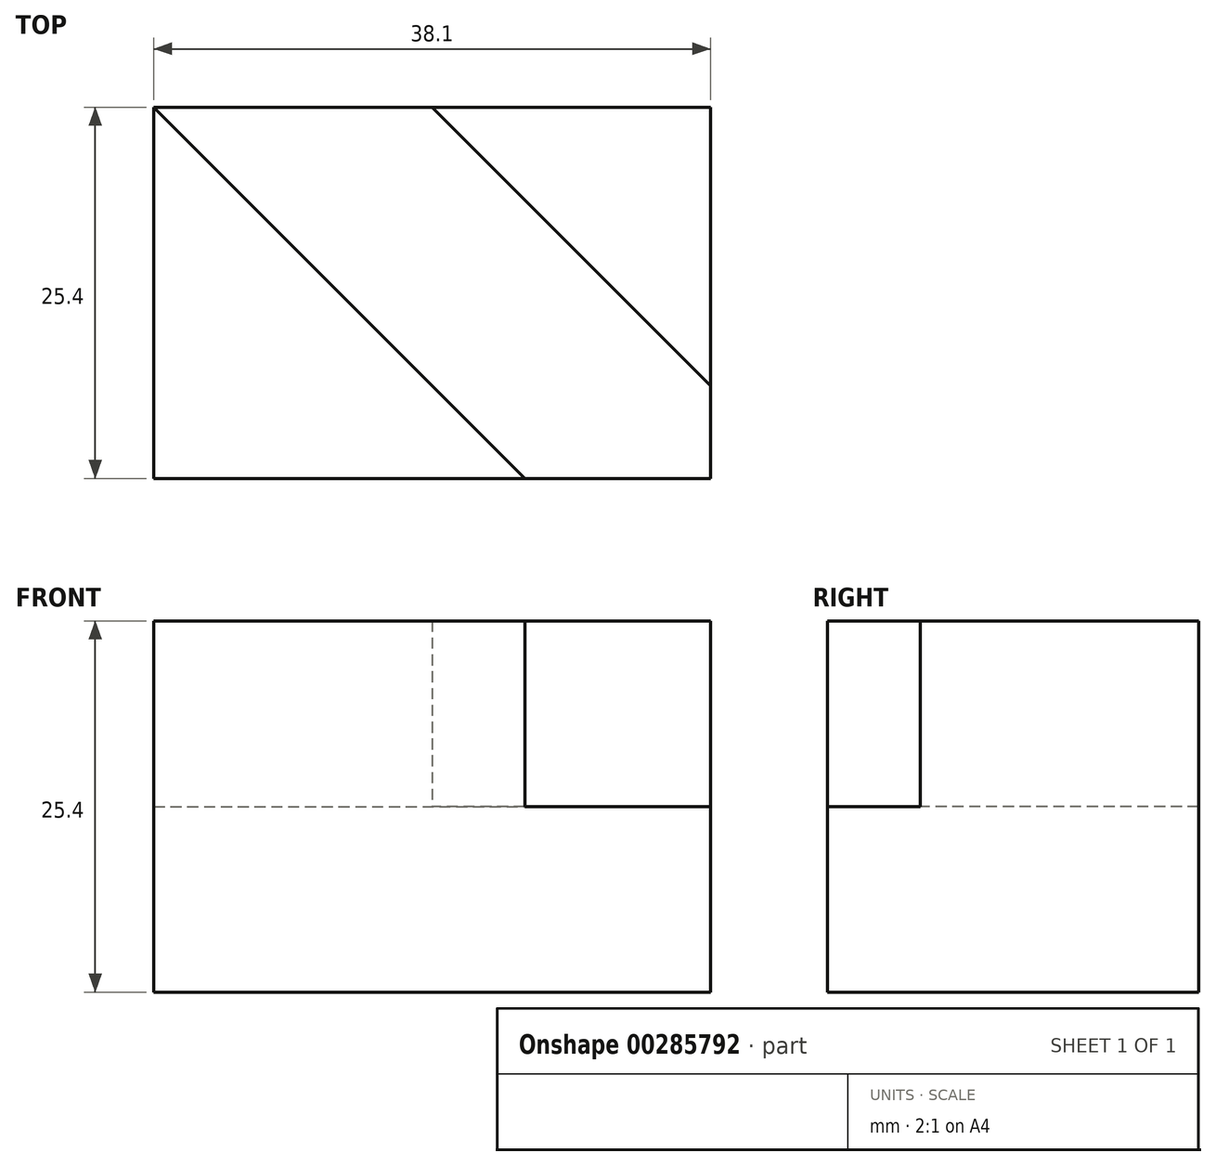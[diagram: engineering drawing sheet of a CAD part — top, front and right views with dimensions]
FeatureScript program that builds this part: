
annotation { "Feature Type Name" : "Feature", "Feature Type Description" : "" }
export const myFeature = defineFeature(function(context is Context, id is Id, definition is map)
    precondition{}
    {
        {
            var Q0;
            Q0=qCreatedBy(makeId("Top.planeOp"),FACE);
            var sketch = newSketch(context, id + "F0", { "sketchPlane" : qUnion([Q0])});
            skLineSegment(sketch, "E0.bottom", {"start": v(0, 0) * mm, "end": v(38.1, 0) * mm});
            skLineSegment(sketch, "E0.top", {"start": v(0, 25.4) * mm, "end": v(38.1, 25.4) * mm});
            skLineSegment(sketch, "E0.left", {"start": v(0, 0) * mm, "end": v(0, 25.4) * mm});
            skLineSegment(sketch, "E0.right", {"start": v(38.1, 0) * mm, "end": v(38.1, 25.4) * mm});
            skLineSegment(sketch, "E1", {"start": v(38.1, 0) * mm, "end": v(25.4, 0) * mm, "construction": true});
            skLineSegment(sketch, "E2", {"start": v(38.1, 0) * mm, "end": v(38.1, 6.35) * mm, "construction": true});
            skLineSegment(sketch, "E3", {"start": v(0, 25.4) * mm, "end": v(25.4, 0) * mm});
            skLineSegment(sketch, "E4", {"start": v(38.1, 6.35) * mm, "end": v(19.05, 25.4) * mm});
            skSolve(sketch);
        }
        {
            var Q0;
            {var subQ4=sQuery(id+"F0.wireOp",EDGE,"E3");Q0=makeQuery(id+"F0.imprint","IMPRINT",FACE,{"disambiguationData":[TD([[makeQuery(id+"F0.imprint","IMPRINT",EDGE,{"derivedFrom":subQ4}),1.0]])]});}
            extrude(context, id + "F1", {"entities" : qUnion([Q0]), "depth" : 12.7 * mm});
        }
        {
            var Q0;
            {var subQ0=sQuery(id+"F0.wireOp",EDGE,"E0.left");Q0=makeQuery(id+"F0.imprint","IMPRINT",FACE,{"disambiguationData":[TD([[makeQuery(id+"F0.imprint","IMPRINT",EDGE,{"derivedFrom":subQ0}),-1.0]])]});}
            var Q1;
            {var subQ3=sQuery(id+"F0.wireOp",EDGE,"E4");Q1=makeQuery(id+"F0.imprint","IMPRINT",FACE,{"disambiguationData":[TD([[makeQuery(id+"F0.imprint","IMPRINT",EDGE,{"derivedFrom":subQ3}),-1.0]])]});}
            extrude(context, id + "F2", {"entities" : qUnion([Q0, Q1]), "operationType" : NewBodyOperationType.ADD, "depth" : 25.4 * mm});
        }
    });
